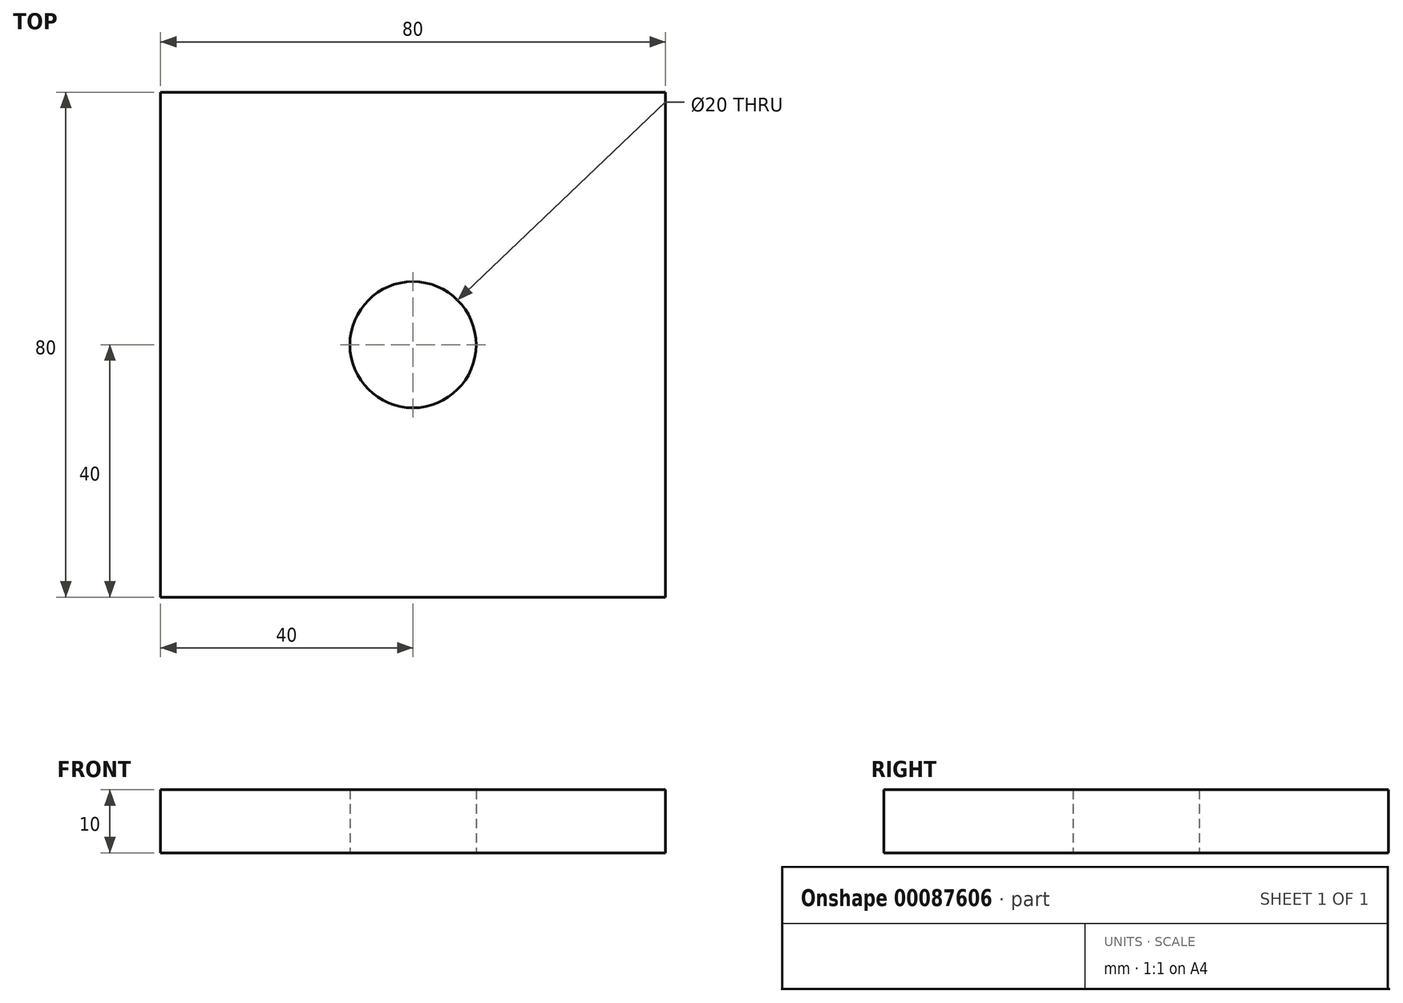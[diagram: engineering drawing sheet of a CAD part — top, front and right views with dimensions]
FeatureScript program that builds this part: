
annotation { "Feature Type Name" : "Feature", "Feature Type Description" : "" }
export const myFeature = defineFeature(function(context is Context, id is Id, definition is map)
    precondition{}
    {
        {
            var Q0;
            Q0=qCreatedBy(makeId("Top.planeOp"),FACE);
            var sketch = newSketch(context, id + "F0", { "sketchPlane" : qUnion([Q0])});
            skLineSegment(sketch, "E0.bottom", {"start": v(0, 0) * mm, "end": v(80, 0) * mm});
            skLineSegment(sketch, "E0.top", {"start": v(0, 80) * mm, "end": v(80, 80) * mm});
            skLineSegment(sketch, "E0.left", {"start": v(0, 0) * mm, "end": v(0, 80) * mm});
            skLineSegment(sketch, "E0.right", {"start": v(80, 0) * mm, "end": v(80, 80) * mm});
            skCircle(sketch, "E1", {"center": v(40, 40) * mm, "radius": 10 * mm});
            skSolve(sketch);
        }
        {
            var Q0;
            Q0 = qSketchRegion(id + "F0", true);
            extrude(context, id + "F1", {"entities" : qUnion([Q0]), "depth" : 10 * mm});
        }
    });
